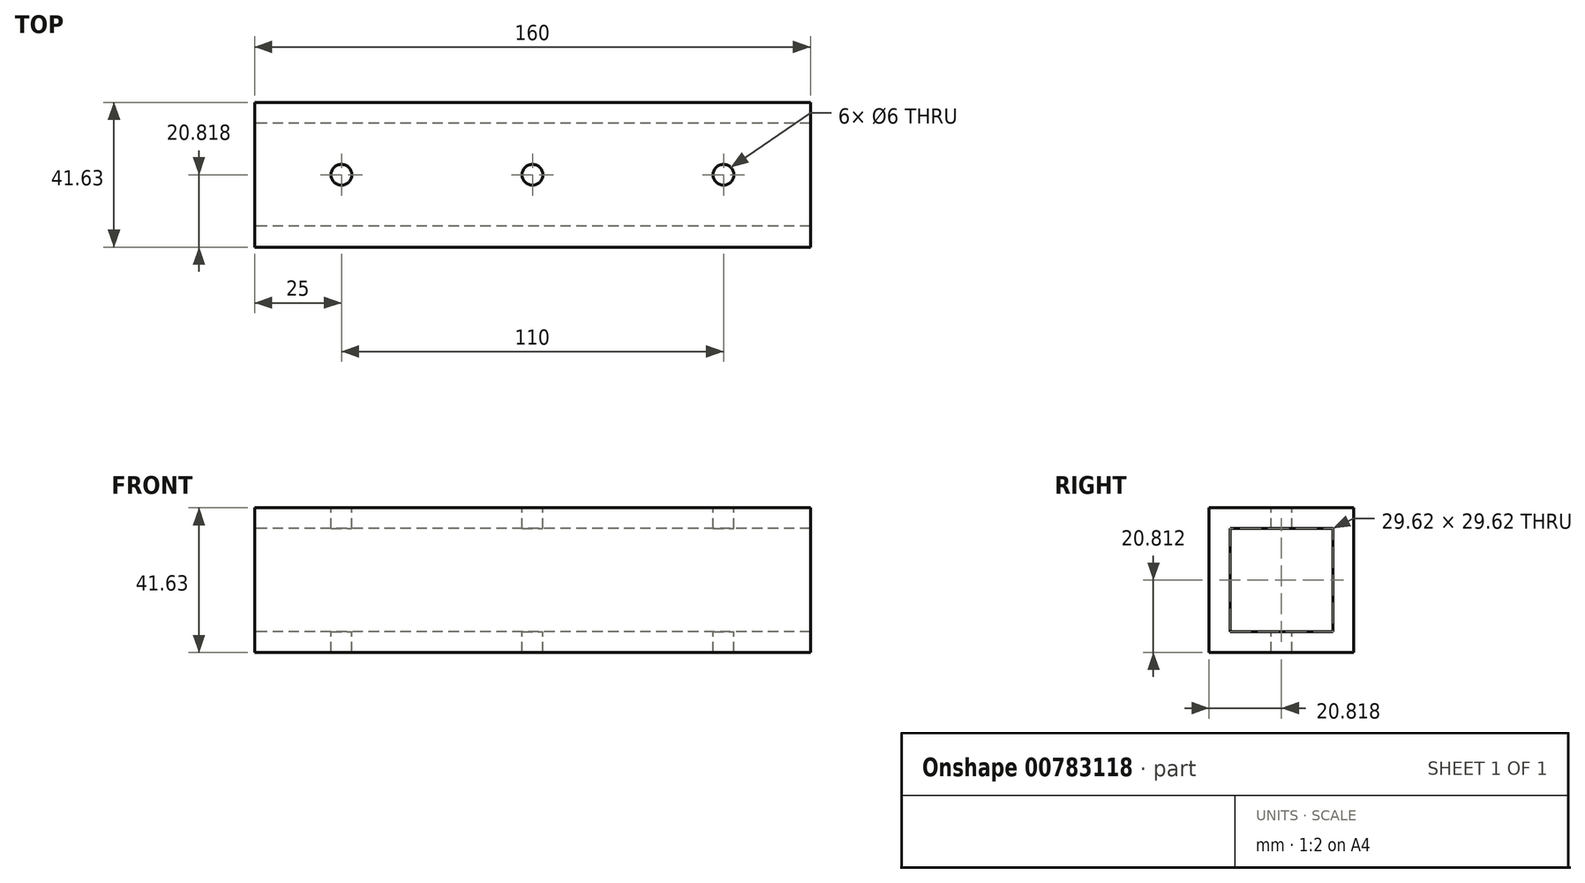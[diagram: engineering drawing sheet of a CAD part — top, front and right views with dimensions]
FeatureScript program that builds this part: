
annotation { "Feature Type Name" : "Feature", "Feature Type Description" : "" }
export const myFeature = defineFeature(function(context is Context, id is Id, definition is map)
    precondition{}
    {
        {
            var Q0;
            Q0=qCreatedBy(makeId("Right.planeOp"),FACE);
            var sketch = newSketch(context, id + "F0", { "sketchPlane" : qUnion([Q0])});
            skLineSegment(sketch, "E0.bottom", {"start": v(0, 0) * mm, "end": v(-41.63, 0) * mm});
            skLineSegment(sketch, "E0.top", {"start": v(0, 41.63) * mm, "end": v(-41.63, 41.63) * mm});
            skLineSegment(sketch, "E0.left", {"start": v(0, 0) * mm, "end": v(0, 41.63) * mm});
            skLineSegment(sketch, "E0.right", {"start": v(-41.63, 0) * mm, "end": v(-41.63, 41.63) * mm});
            skLineSegment(sketch, "E1.0", {"start": v(-6, 35.63) * mm, "end": v(-35.63, 35.63) * mm});
            skLineSegment(sketch, "E1.1", {"start": v(-6, 6) * mm, "end": v(-6, 35.63) * mm});
            skLineSegment(sketch, "E1.2", {"start": v(-6, 6) * mm, "end": v(-35.63, 6) * mm});
            skLineSegment(sketch, "E1.3", {"start": v(-35.63, 6) * mm, "end": v(-35.63, 35.63) * mm});
            skSolve(sketch);
        }
        {
            var Q0;
            Q0=makeQuery(id+"F0.imprint","IMPRINT",FACE,{"disambiguationData":[TD([[makeQuery(id+"F0.imprint","IMPRINT",EDGE,{"derivedFrom":sQuery(id+"F0.wireOp",EDGE,"E0.bottom")}),-1.0]])]});
            extrude(context, id + "F1", {"entities" : qUnion([Q0]), "depth" : 160 * mm, "offsetDistance" : 25 * mm});
        }
        {
            var Q0;
            Q0=makeQuery(id+"F1.opExtrude","SWEPT_FACE",FACE,{"disambiguationData":[OSD([sQuery(id+"F0.wireOp",EDGE,"E0.top")])]});
            var sketch = newSketch(context, id + "F2", { "sketchPlane" : qUnion([Q0])});
            skCircle(sketch, "E2", {"center": v(80, -20.81) * mm, "radius": 3 * mm});
            skPoint(sketch, "E2.centerSnap0", {"position": v(80, 0) * mm});
            skPoint(sketch, "E2.centerSnap1", {"position": v(0, -20.81) * mm});
            skCircle(sketch, "E3", {"center": v(25, -20.81) * mm, "radius": 3 * mm});
            skCircle(sketch, "E4", {"center": v(135, -20.81) * mm, "radius": 3 * mm});
            skSolve(sketch);
        }
        {
            var Q0;
            Q0=sQuery(id+"F2.wireOp",VERTEX,"E4.center");
            var Q1;
            Q1=sQuery(id+"F2.wireOp",VERTEX,"E2.center");
            var Q2;
            Q2=sQuery(id+"F2.wireOp",VERTEX,"E3.center");
            var Q3;
            Q3=makeQuery(id+"F1.opExtrude","SWEPT_BODY",BODY,{"disambiguationData":[OSD([sQuery(id+"F0.wireOp",EDGE,"E0.bottom"),sQuery(id+"F0.wireOp",EDGE,"E0.top"),sQuery(id+"F0.wireOp",EDGE,"E0.left"),sQuery(id+"F0.wireOp",EDGE,"E0.right"),sQuery(id+"F0.wireOp",EDGE,"E1.0"),sQuery(id+"F0.wireOp",EDGE,"E1.1"),sQuery(id+"F0.wireOp",EDGE,"E1.2"),sQuery(id+"F0.wireOp",EDGE,"E1.3")])]});
            hole(context, id + "F3", {"style" : HoleStyle.SIMPLE, "endStyle" : HoleEndStyle.THROUGH, "holeDiameter" : 6 * mm, "majorDiameter" : 5 * mm, "isTappedThrough" : true, "tappedDepth" : 12 * mm, "tapClearance" : 3, "locations" : qUnion([Q0, Q1, Q2]), "scope" : qUnion([Q3])});
        }
    });
